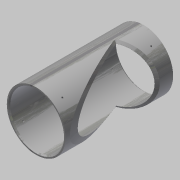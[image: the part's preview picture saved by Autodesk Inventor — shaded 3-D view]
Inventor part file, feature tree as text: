
AUTODESK INVENTOR PART (.ipt)
format: ipt  version: 2017.3 (Build 213257000, 257)  size: 398,336 bytes
history: native  units: in
note: dims shown in document units (in); Inventor stores cm internally (conversion verified against a paired STEP export)
features: other x14, extrude x8, split x8, plane x7, sketch x5, loft x4, chamfer x2, hole x2, pattern_circular x1
ambient origin geometry x8: Origin, YZ Plane, XZ Plane, XY Plane, X Axis, Y Axis, Z Axis, Center Point
bodies: Solid1 (feature_tree)
feature tree (51):
  sketch  "Sketch1"  dims[d0=34.25in d1=37.25in]
  extrude  "Extrusion1"  Depth=37.25in
  sketch  "Sketch2"  dims[d2=50.9606in d3=17.4961in d4=0.0in d5=0.0in d6=22.5deg]
  extrude  "Extrusion2"  TaperAngle=22.5deg  [1 undecoded]
  split  "Split1"
  split  "Split2"
  plane  "Work Plane1"
  plane  "Work Plane2"
  split  "Split3"
  split  "Split4"
  loft  "Loft1"
  loft  "Loft2"
  loft  "Loft3"
  loft  "Loft4"
  chamfer  "Chamfer1"  Angle=90.0deg  [1 undecoded]
  chamfer  "Chamfer2"  Angle=90.0deg  [1 undecoded]
  sketch  "Sketch3"  dims[d7=0.0938in d8=70.0in d9=0.0in]
  plane  "Work Plane3"
  plane  "Work Plane4"
  plane  "Work Plane5"
  plane  "Work Plane6"
  plane  "Work Plane7"
  hole  "Hole1"  [1 undecoded]
  hole  "Hole2"  [1 undecoded]
  pattern_circular  "Circular Pattern1"  Angle=90.0deg  [1 undecoded]
  split  "Split5"
  split  "Split6"
  split  "Split7"
  split  "Split8"
  other  "Srf1"
  other  "Srf2"
  other  "Edges1"
  other  "Edges2"
  other  "Edges3"
  other  "Edges4"
  other  "Edges5"
  other  "Edges6"
  other  "Edges7"
  other  "Edges8"
  sketch  "Sketch4"  dims[d10=34.375in d11=0.0in d12=0.0in]
  sketch  "Sketch5"  dims[d13=1.103in d14=70.0in d15=0.0in d16=22.5deg d17=22.5deg d18=0.0in d19=90.0deg d20=0.0in d21=90.0deg d22=0.0in d23=90.0deg d24=0.0in d25=90.0deg d26=0.0in d27=90.0deg d28=0.0in d29=90.0deg d30=0.0in d31=90.0deg d32=0.0in d33=90.0deg d34=0.75in d35=0.125in d36=0.2749in d37=0.75in d38=0.125in d39=0.2749in d40=75.0deg d41=0.0938in d42=0.0469in d43=0.0687in d46=0.0687in d47=135.0deg d48=-0.9276in d49=6.0in d50=6.0in d51=0.891in d52=0.553in d53=0.0246in d54=0.897in d55=0.375in d56=0.25in d57=0.5635in d58=3.0in d59=0.8108in d60=6.0in d61=6.0in d62=0.891in d63=0.553in d64=0.0246in d65=0.897in d66=0.375in d67=0.25in d68=0.5635in d69=3.0in d70=0.8108in d71=0.7874in d72=1.0994in d74=0.0in d75=0.0in d76=0.0in d77=0.0in]
  other  "Srf3"
  other  "Srf4"
  other  "Srf5"
  other  "Srf6"
  extrude  "ExtrusionSrf1"  TaperAngle=0.0deg  [1 undecoded]
  extrude  "ExtrusionSrf2"  TaperAngle=0.0deg  [1 undecoded]
  extrude  "ExtrusionSrf3"  TaperAngle=0.0deg  [1 undecoded]
  extrude  "ExtrusionSrf4"  Depth=0.0938in
  extrude  "ExtrusionSrf5"  Depth=0.0938in
  extrude  "ExtrusionSrf6"  TaperAngle=75.0deg  [1 undecoded]
note: 10 required parameter values undecoded (feature->parameter linkage not recoverable at this tier; creation-order binding heuristic only, values carry confidence <= 0.55)
